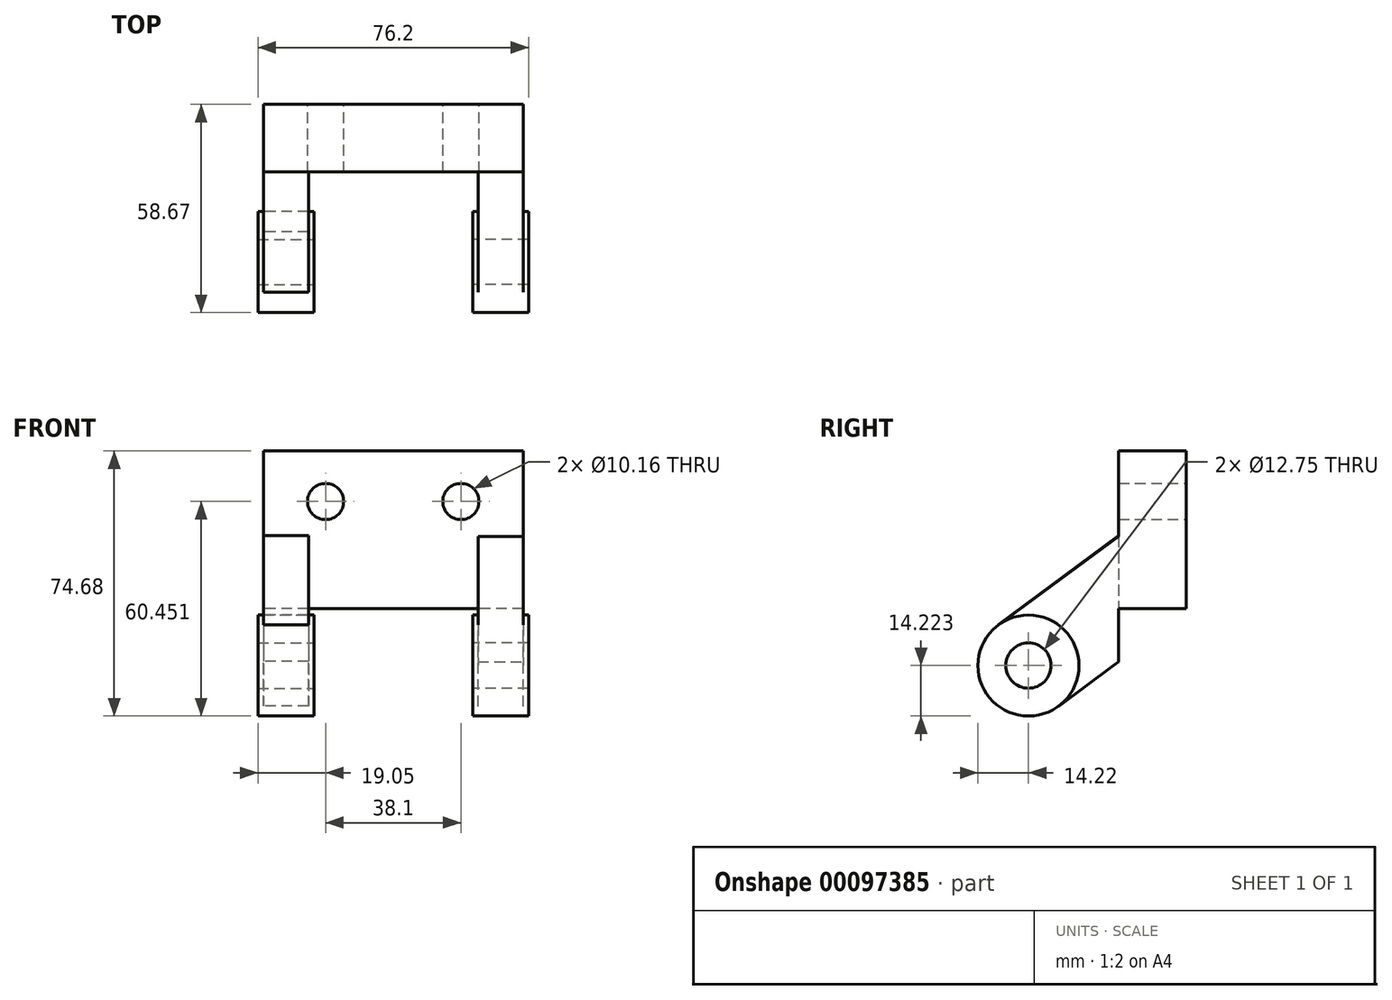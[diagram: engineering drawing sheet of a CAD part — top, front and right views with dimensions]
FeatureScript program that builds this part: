
annotation { "Feature Type Name" : "Feature", "Feature Type Description" : "" }
export const myFeature = defineFeature(function(context is Context, id is Id, definition is map)
    precondition{}
    {
        {
            var Q0;
            Q0=qCreatedBy(makeId("Front.planeOp"),FACE);
            var sketch = newSketch(context, id + "F0", { "sketchPlane" : qUnion([Q0])});
            skLineSegment(sketch, "E0.bottom", {"start": v(36.58, 22.23) * mm, "end": v(-36.58, 22.23) * mm});
            skLineSegment(sketch, "E0.top", {"start": v(36.58, -22.23) * mm, "end": v(-36.58, -22.23) * mm});
            skLineSegment(sketch, "E0.left", {"start": v(36.58, 22.23) * mm, "end": v(36.58, -22.23) * mm});
            skLineSegment(sketch, "E0.right", {"start": v(-36.58, 22.23) * mm, "end": v(-36.58, -22.23) * mm});
            skPoint(sketch, "E0.middle", {"position": v(0, 0) * mm});
            skPoint(sketch, "E1", {"position": v(19.05, 8) * mm});
            skPoint(sketch, "E2", {"position": v(-19.05, 8) * mm});
            skCircle(sketch, "E3", {"center": v(19.05, 8) * mm, "radius": 5.08 * mm});
            skCircle(sketch, "E4", {"center": v(-19.05, 8) * mm, "radius": 5.08 * mm});
            skSolve(sketch);
        }
        {
            var Q0;
            Q0 = qSketchRegion(id + "F0", true);
            extrude(context, id + "F1", {"entities" : qUnion([Q0]), "depth" : 19.05 * mm});
        }
        {
            var Q0;
            Q0=makeQuery(id+"F1.opExtrude","SWEPT_FACE",FACE,{"disambiguationData":[OSD([sQuery(id+"F0.wireOp",EDGE,"E0.left")])]});
            var sketch = newSketch(context, id + "F2", { "sketchPlane" : qUnion([Q0])});
            skLineSegment(sketch, "E5", {"start": v(0, 22.23) * mm, "end": v(0, 8) * mm});
            skLineSegment(sketch, "E6", {"start": v(0, 8) * mm, "end": v(0, -38.23) * mm});
            skLineSegment(sketch, "E7", {"start": v(0, -38.23) * mm, "end": v(-44.45, -38.23) * mm});
            skCircle(sketch, "E8", {"center": v(-44.45, -38.23) * mm, "radius": 14.22 * mm});
            skCircle(sketch, "E9", {"center": v(-44.45, -38.23) * mm, "radius": 6.38 * mm});
            skLineSegment(sketch, "E10", {"start": v(-52.88, -26.77) * mm, "end": v(-19.05, -1.86) * mm});
            skLineSegment(sketch, "E11", {"start": v(-36.02, -49.68) * mm, "end": v(-20.46, -38.23) * mm});
            skLineSegment(sketch, "E12", {"start": v(-19.05, -1.86) * mm, "end": v(-19.05, -37.19) * mm});
            skLineSegment(sketch, "E13", {"start": v(-19.05, -37.19) * mm, "end": v(-20.46, -38.23) * mm});
            skSolve(sketch);
        }
        {
            var Q0;
            {var subQ0=sQuery(id+"F2.wireOp",EDGE,"E11");Q0=makeQuery(id+"F2.imprint","IMPRINT",FACE,{"disambiguationData":[TD([[makeQuery(id+"F2.imprint","IMPRINT",EDGE,{"derivedFrom":subQ0}),1.0]])]});}
            var Q1;
            {var subQ4=sQuery(id+"F2.wireOp",EDGE,"E10");Q1=makeQuery(id+"F2.imprint","IMPRINT",FACE,{"disambiguationData":[TD([[makeQuery(id+"F2.imprint","IMPRINT",EDGE,{"derivedFrom":subQ4}),-1.0]])]});}
            extrude(context, id + "F3", {"entities" : qUnion([Q0, Q1]), "operationType" : NewBodyOperationType.ADD, "oppositeDirection" : true, "depth" : 12.7 * mm});
        }
        {
            var Q0;
            Q0=makeQuery(id+"F2.imprint","IMPRINT",FACE,{"disambiguationData":[TD([[makeQuery(id+"F2.imprint","IMPRINT",EDGE,{"derivedFrom":sQuery(id+"F2.wireOp",EDGE,"E9")}),-1.0]])]});
            extrude(context, id + "F4", {"entities" : qUnion([Q0]), "operationType" : NewBodyOperationType.ADD, "depth" : 1.52 * mm, "hasSecondDirection" : true, "secondDirectionOppositeDirection" : true, "secondDirectionDepth" : 14.22 * mm});
        }
        {
            var Q0;
            Q0=makeQuery(id+"F1.opExtrude","SWEPT_FACE",FACE,{"disambiguationData":[OSD([sQuery(id+"F0.wireOp",EDGE,"E0.right")])]});
            var sketch = newSketch(context, id + "F5", { "sketchPlane" : qUnion([Q0])});
            skLineSegment(sketch, "E14", {"start": v(0, 22.22) * mm, "end": v(0, 8) * mm});
            skLineSegment(sketch, "E15", {"start": v(0, 8) * mm, "end": v(0, -38.23) * mm});
            skLineSegment(sketch, "E16", {"start": v(0, -38.23) * mm, "end": v(44.45, -38.23) * mm});
            skCircle(sketch, "E17", {"center": v(44.45, -38.23) * mm, "radius": 6.38 * mm});
            skCircle(sketch, "E18", {"center": v(44.45, -38.23) * mm, "radius": 14.22 * mm});
            skLineSegment(sketch, "E19", {"start": v(52.93, -26.8) * mm, "end": v(19.05, -1.63) * mm});
            skLineSegment(sketch, "E20", {"start": v(35.97, -49.64) * mm, "end": v(19.04, -37.07) * mm});
            skLineSegment(sketch, "E21", {"start": v(19.05, -1.63) * mm, "end": v(19.04, -37.07) * mm});
            skSolve(sketch);
        }
        {
            var Q0;
            {var subQ0=sQuery(id+"F5.wireOp",EDGE,"E20");var subQ1=sQuery(id+"F5.wireOp",EDGE,"E16");var subQ2=makeQuery(id+"F5.imprint","INTERSECT",VERTEX,{"derivedFrom":[subQ1,subQ0]});Q0=makeQuery(id+"F5.imprint","IMPRINT",FACE,{"disambiguationData":[TD([[makeQuery(id+"F5.imprint","IMPRINT",EDGE,{"disambiguationData":[TD([[subQ2,-1.0]])],"derivedFrom":subQ1}),-1.0]])]});}
            var Q1;
            {var subQ11=sQuery(id+"F5.wireOp",EDGE,"E19");Q1=makeQuery(id+"F5.imprint","IMPRINT",FACE,{"disambiguationData":[TD([[makeQuery(id+"F5.imprint","IMPRINT",EDGE,{"derivedFrom":subQ11}),1.0]])]});}
            extrude(context, id + "F6", {"entities" : qUnion([Q0, Q1]), "oppositeDirection" : true, "depth" : 12.7 * mm});
        }
        {
            var Q0;
            Q0=makeQuery(id+"F5.imprint","IMPRINT",FACE,{"disambiguationData":[TD([[makeQuery(id+"F5.imprint","IMPRINT",EDGE,{"derivedFrom":sQuery(id+"F5.wireOp",EDGE,"E17")}),-1.0]])]});
            extrude(context, id + "F7", {"entities" : qUnion([Q0]), "depth" : 1.52 * mm, "hasSecondDirection" : true, "secondDirectionOppositeDirection" : true, "secondDirectionDepth" : 14.22 * mm});
        }
    });
